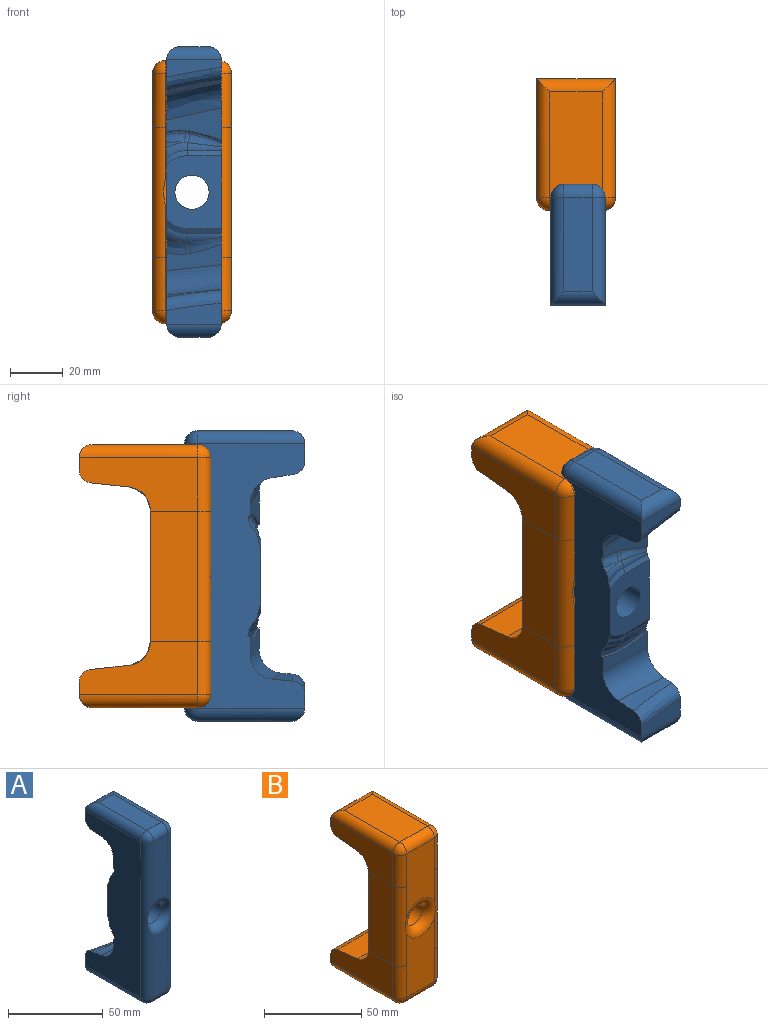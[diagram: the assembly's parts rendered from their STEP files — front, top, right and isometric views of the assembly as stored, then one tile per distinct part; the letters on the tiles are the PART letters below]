
ASSEMBLY  parts=2 mates=1
PART A: 63 faces, bbox 73.3x52x116.5 mm
  f0: plane 40.47x10.7mm, normal (0,-1,0), area 419.2mm2, adj f51,f52,f56,f59
  f1: plane 35.8x10.7mm, normal (0,0,1), area 383.1mm2, adj f46,f49,f54,f55
  f2: plane 35.8x10.7mm, normal (0,0,-1), area 383.1mm2, adj f45,f48,f52,f53
  f3: plane 40.36x10.7mm, normal (0,-1,0), area 418mm2, adj f51,f55,f56,f59
  f4: cylinder r=251mm len=17.53mm, axis (-0.02,0.99,-0.12), area 24.2mm2, adj f7,f44,f61
  f5: cylinder r=200mm len=22.3mm, axis (0.13,0.99,0.07), area 126.5mm2, adj f12,f24,f44,f62
  f6: plane 27.73x20.74mm, normal (0,1,0), area 423.2mm2, adj f21,f22,f24,f28,f38,f39,f44
  f7: offset ~32.93x18.13mm, area 106.5mm2, adj f4,f13,f24,f44,f60
  f8: offset ~16.3x9.94mm, area 25.8mm2, adj f19,f23,f36,f44
  f9: plane 20.79x12.41mm, normal (-0.16,0.99,0), area 155.8mm2, adj f14,f23,f24,f42,f43,f44
  f10: plane 21.2x10.66mm, normal (-0.16,0.99,0), area 127.9mm2, adj f11,f15,f24,f29,f30,f44
  f11: bspline ~25.1x4.25mm, area 4.2mm2, adj f10,f12,f24,f44
  f12: offset ~37.32x14.96mm, area 290.4mm2, adj f5,f11,f24,f44
  f13: offset ~67.87x19.12mm, area 299.6mm2, adj f7,f14,f24,f44
  f14: bspline ~25.1x5.57mm, area 4.3mm2, adj f9,f13,f24,f44
  f15: bspline ~9.74x2.55mm, area 7.4mm2, adj f10,f17,f29,f44
  f16: cone r=15.71mm half-angle=50deg, axis (0,-1,0), area 7.5mm2, adj f17,f18,f44
  f17: offset ~16.31x9.96mm, area 34.4mm2, adj f15,f16,f33,f44
  f18: torus R=12.84mm, axis (0,-1,0), area 28.4mm2, adj f16,f22,f27,f33,f34,f44
  f19: cone r=15.71mm half-angle=50deg, axis (0,-1,0), area 7.5mm2, adj f8,f20,f44
  f20: torus R=12.84mm, axis (0,-1,0), area 25.2mm2, adj f19,f21,f26,f36,f37,f44
  f21: bspline ~9.48x5.52mm, area 19.8mm2, adj f6,f20,f38,f44
  f22: bspline ~9.48x5.52mm, area 19.8mm2, adj f6,f18,f39,f44
  f23: bspline ~7.71x2.1mm, area 12.2mm2, adj f8,f9,f42,f44
  f24: plane 101.14x41.61mm, normal (1,0,0), area 2761.8mm2, adj f5,f6,f7,f9,f10,f11,f12,f13
  f25: bspline ~0.8x0.66mm, area 0mm2, adj f36,f37
  f26: cylinder r=4.82mm len=12.72mm, axis (1,0,0), area 30.2mm2, adj f20,f24,f35,f38
  f27: cylinder r=4.82mm len=12.73mm, axis (1,0,0), area 30mm2, adj f18,f24,f32,f39
  f28: cylinder r=6.5mm len=24.07mm, axis (0,1,0), area 982.9mm2, adj f6,f56
  f29: bspline ~1.96x1.29mm, area 1.8mm2, adj f10,f15,f30,f33
  f30: bspline ~11.87x3.53mm, area 12.3mm2, adj f10,f24,f29,f32
  f31: bspline ~1.52x0.93mm, area 0mm2, adj f33,f34
  f32: offset ~20.72x11.82mm, area 47mm2, adj f24,f27,f30,f33
  f33: cylinder r=7.21mm len=4.89mm, axis (0.98,0.16,-0.15), area 7.8mm2, adj f17,f18,f29,f31,f32
  f34: bspline ~0.77x0.64mm, area 0mm2, adj f18,f31
  f35: offset ~20.54x11.78mm, area 31.1mm2, adj f24,f26,f36,f43
  f36: cylinder r=7.21mm len=3.73mm, axis (0.98,0.16,0.15), area 6.1mm2, adj f8,f20,f25,f35,f42
  f37: bspline ~5.07x1.78mm, area 0.1mm2, adj f20,f25
  f38: plane 12.7x2mm, normal (0,0.89,-0.45), area 28.4mm2, adj f6,f21,f24,f26
  f39: plane 12.7x2mm, normal (0,0.89,0.45), area 28.4mm2, adj f6,f22,f24,f27
  f40: plane 20.7x7.89mm, normal (0,1,0), area 139.2mm2, adj f24,f44,f49,f62
  f41: plane 20.7x6.57mm, normal (0,1,0), area 93.9mm2, adj f24,f44,f48,f60,f61
  f42: bspline ~1.86x1.42mm, area 3mm2, adj f9,f23,f36,f43
  f43: bspline ~14.11x5.27mm, area 20.6mm2, adj f9,f24,f35,f42
  f44: plane 101.41x41.88mm, normal (-1,0,0), area 2639.8mm2, adj f4,f5,f6,f7,f8,f9,f10,f11
  f45: cylinder r=5mm len=40.8mm, axis (0,-1,0), area 300.8mm2, adj f2,f24,f47,f48
  f46: cylinder r=5mm len=40.8mm, axis (0,-1,0), area 300.8mm2, adj f1,f24,f49,f50
  f47: sphere r=5mm, area 39.3mm2, adj f45,f51,f52
  f48: cylinder r=5mm len=20.7mm, axis (1,0,0), area 123.3mm2, adj f2,f41,f45,f53
  f49: cylinder r=5mm len=20.7mm, axis (-1,0,0), area 123.3mm2, adj f1,f40,f46,f54
  f50: sphere r=5mm, area 39.3mm2, adj f46,f51,f55
  f51: cylinder r=5mm len=100.33mm, axis (0,0,1), area 751.5mm2, adj f0,f3,f24,f47,f50,f56
  f52: cylinder r=5mm len=10.7mm, axis (-1,0,0), area 84mm2, adj f0,f2,f47,f57
  f53: cylinder r=5mm len=40.8mm, axis (0,1,0), area 300.8mm2, adj f2,f44,f48,f57
  f54: cylinder r=5mm len=40.8mm, axis (0,-1,0), area 300.8mm2, adj f1,f44,f49,f58
  f55: cylinder r=5mm len=10.7mm, axis (1,0,0), area 84mm2, adj f1,f3,f50,f58
  f56: torus R=11.5mm, axis (0,1,0), area 309.9mm2, adj f0,f3,f28,f51,f59
  f57: sphere r=5mm, area 39.3mm2, adj f52,f53,f59
  f58: sphere r=5mm, area 39.3mm2, adj f54,f55,f59
  f59: cylinder r=5mm len=100.33mm, axis (0,0,-1), area 736.3mm2, adj f0,f3,f44,f56,f57,f58
  f60: bspline ~24.13x8.67mm, area 26.6mm2, adj f7,f24,f41,f61
  f61: bspline ~18.53x8.26mm, area 125.2mm2, adj f4,f41,f44,f60
  f62: bspline ~21.98x7.7mm, area 155.5mm2, adj f5,f24,f40,f44
PART B: 39 faces, bbox 33.2x50.6x100.6 mm
  f0: plane 39.32x20mm, normal (0,-1,0), area 703.8mm2, adj f21,f22,f24,f27,f28,f30
  f1: plane 45.01x20.31mm, normal (1,0,0), area 658.9mm2, adj f4,f9,f13,f14,f33,f36,f38
  f2: plane 45.01x20.31mm, normal (1,0,0), area 659.1mm2, adj f9,f12,f16,f17,f23,f28,f37
  f3: plane 45.02x20.32mm, normal (-1,0,0), area 659.1mm2, adj f8,f12,f16,f17,f18,f21,f37
  f4: plane 30x4.59mm, normal (0,1,0), area 137.7mm2, adj f1,f6,f34,f38
  f5: plane 40x20mm, normal (0,0,-1), area 800mm2, adj f31,f32,f34,f36
  f6: plane 45.03x20.33mm, normal (-1,0,0), area 659mm2, adj f4,f8,f13,f14,f26,f31,f38
  f7: plane 40x20mm, normal (0,0,1), area 800mm2, adj f18,f20,f22,f23
  f8: plane 49.4x17.9mm, normal (-1,0,0), area 884.2mm2, adj f3,f6,f15,f24
  f9: plane 49.4x17.9mm, normal (1,0,0), area 884.3mm2, adj f1,f2,f15,f30
  f10: cylinder r=6.5mm len=17.9mm, axis (0,1,0), area 731mm2, adj f15,f27
  f11: plane 39.32x20mm, normal (0,-1,0), area 703.8mm2, adj f24,f26,f27,f30,f32,f33
  f12: plane 30x4.59mm, normal (0,1,0), area 137.7mm2, adj f2,f3,f20,f37
  f13: plane 30x14.56mm, normal (0,0.11,0.99), area 439.3mm2, adj f1,f6,f14,f38
  f14: extruded ~30x9.16mm, area 401.2mm2, adj f1,f6,f13,f15
  f15: plane 49.4x30mm, normal (0,1,0), area 1349.2mm2, adj f8,f9,f10,f14,f16
  f16: extruded ~30x9.16mm, area 401.4mm2, adj f2,f3,f15,f17
  f17: plane 30.64x15.19mm, normal (0,0.11,-0.99), area 439mm2, adj f2,f3,f16,f37
  f18: cylinder r=5mm len=45mm, axis (0,1,0), area 333.8mm2, adj f3,f7,f19,f20
  f19: sphere r=5mm, area 39.3mm2, adj f18,f21,f22
  f20: cylinder r=5mm len=30mm, axis (-1,0,0), area 196.3mm2, adj f7,f12,f18,f23
  f21: cylinder r=5mm len=20.3mm, axis (0,0,1), area 159.4mm2, adj f0,f3,f19,f24
  f22: cylinder r=5mm len=20mm, axis (1,0,0), area 157.1mm2, adj f0,f7,f19,f25
  f23: cylinder r=5mm len=45mm, axis (0,-1,0), area 333.8mm2, adj f2,f7,f20,f25
  f24: cylinder r=5mm len=49.4mm, axis (0,0,1), area 382.3mm2, adj f0,f8,f11,f21,f26,f27
  f25: sphere r=5mm, area 39.3mm2, adj f22,f23,f28
  f26: cylinder r=5mm len=20.3mm, axis (0,0,-1), area 159.4mm2, adj f6,f11,f24,f29
  f27: torus R=11.5mm, axis (0,-1,0), area 400.2mm2, adj f0,f10,f11,f24,f30
  f28: cylinder r=5mm len=20.3mm, axis (0,0,-1), area 159.4mm2, adj f0,f2,f25,f30
  f29: sphere r=5mm, area 39.3mm2, adj f26,f31,f32
  f30: cylinder r=5mm len=49.4mm, axis (0,0,-1), area 383.7mm2, adj f0,f9,f11,f27,f28,f33
  f31: cylinder r=5mm len=45mm, axis (0,1,0), area 333.8mm2, adj f5,f6,f29,f34
  f32: cylinder r=5mm len=20mm, axis (1,0,0), area 157.1mm2, adj f5,f11,f29,f35
  f33: cylinder r=5mm len=20.3mm, axis (0,0,1), area 159.4mm2, adj f1,f11,f30,f35
  f34: cylinder r=5mm len=30mm, axis (-1,0,0), area 196.3mm2, adj f4,f5,f31,f36
  f35: sphere r=5mm, area 39.3mm2, adj f32,f33,f36
  f36: cylinder r=5mm len=45mm, axis (0,-1,0), area 333.8mm2, adj f1,f5,f34,f35
  f37: cylinder r=5mm len=30mm, axis (-1,0,0), area 219.4mm2, adj f2,f3,f12,f17
  f38: cylinder r=5mm len=30mm, axis (1,0,0), area 219.4mm2, adj f1,f4,f6,f13
PLACE A rot(axis=(1,0,0),180deg) t=(107.22,-412.6,-410.91)mm
PLACE B t=(-769.54,-289.58,168.98)mm
MATE cylindrical A.f28 <-> B.f10  axis (0,-1,0) through (-388.67,-325,-120.91)mm
